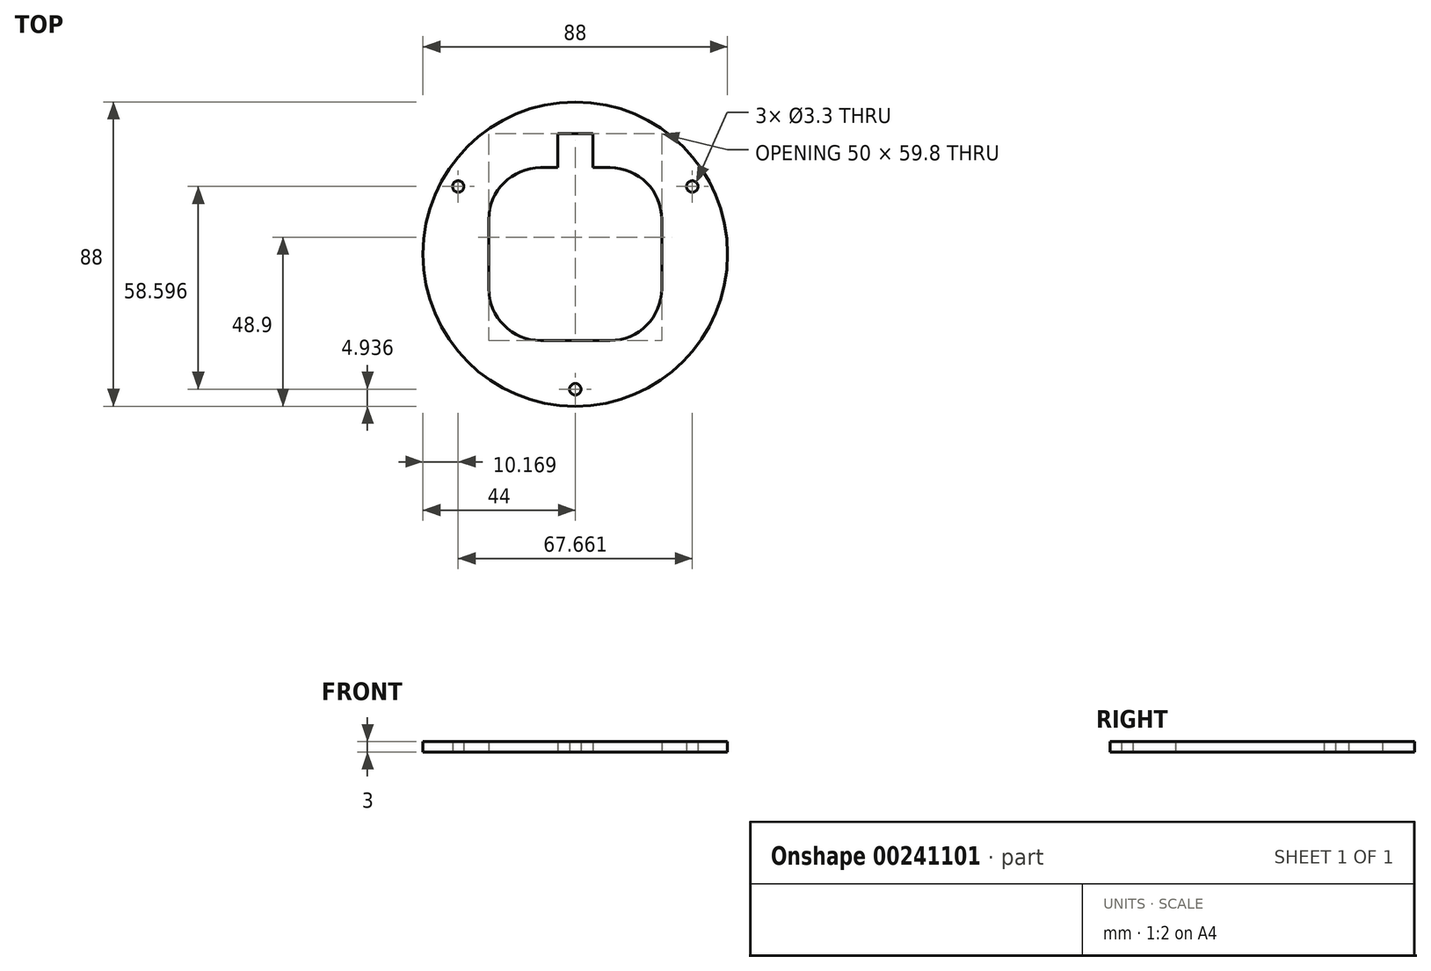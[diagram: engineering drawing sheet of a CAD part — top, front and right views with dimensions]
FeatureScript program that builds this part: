
annotation { "Feature Type Name" : "Feature", "Feature Type Description" : "" }
export const myFeature = defineFeature(function(context is Context, id is Id, definition is map)
    precondition{}
    {
        {
            var Q0;
            Q0=qCreatedBy(makeId("Top.planeOp"),FACE);
            var sketch = newSketch(context, id + "F0", { "sketchPlane" : qUnion([Q0])});
            skCircle(sketch, "E0", {"center": v(0, -39.06) * mm, "radius": 1.65 * mm});
            skCircle(sketch, "E1.1.0", {"center": v(33.83, 19.53) * mm, "radius": 1.65 * mm});
            skCircle(sketch, "E1.2.0", {"center": v(-33.83, 19.53) * mm, "radius": 1.65 * mm});
            skPoint(sketch, "E1.center", {"position": v(0, 0) * mm});
            skCircle(sketch, "E2", {"center": v(0, 0) * mm, "radius": 44 * mm});
            skLineSegment(sketch, "E3.bottom", {"start": v(5.1, 16.8) * mm, "end": v(-5.1, 16.8) * mm});
            skLineSegment(sketch, "E3.top", {"start": v(5.1, 34.8) * mm, "end": v(-5.1, 34.8) * mm});
            skLineSegment(sketch, "E3.left", {"start": v(5.1, 16.8) * mm, "end": v(5.1, 34.8) * mm});
            skLineSegment(sketch, "E3.right", {"start": v(-5.1, 16.8) * mm, "end": v(-5.1, 34.8) * mm});
            skPoint(sketch, "E3.middle", {"position": v(0, 25.8) * mm});
            skLineSegment(sketch, "E4.bottom", {"start": v(10, -25) * mm, "end": v(-10, -25) * mm});
            skLineSegment(sketch, "E4.top", {"start": v(10, 25) * mm, "end": v(-10, 25) * mm});
            skLineSegment(sketch, "E4.left", {"start": v(25, -10) * mm, "end": v(25, 10) * mm});
            skLineSegment(sketch, "E4.right", {"start": v(-25, -10) * mm, "end": v(-25, 10) * mm});
            skArc(sketch, "E5.filletArc", {"start": v(-10, 25) * mm, "mid": v(-20.6, 20.6) * mm, "end": v(-25, 10) * mm});
            skArc(sketch, "E6.filletArc", {"start": v(25, 10) * mm, "mid": v(20.6, 20.6) * mm, "end": v(10, 25) * mm});
            skArc(sketch, "E7.filletArc", {"start": v(10, -25) * mm, "mid": v(20.6, -20.6) * mm, "end": v(25, -10) * mm});
            skArc(sketch, "E8.filletArc", {"start": v(-25, -10) * mm, "mid": v(-20.6, -20.6) * mm, "end": v(-10, -25) * mm});
            skSolve(sketch);
        }
        {
            var Q0;
            Q0 = qSketchRegion(id + "F0", true);
            extrude(context, id + "F1", {"entities" : qUnion([Q0]), "depth" : 3 * mm});
        }
    });
